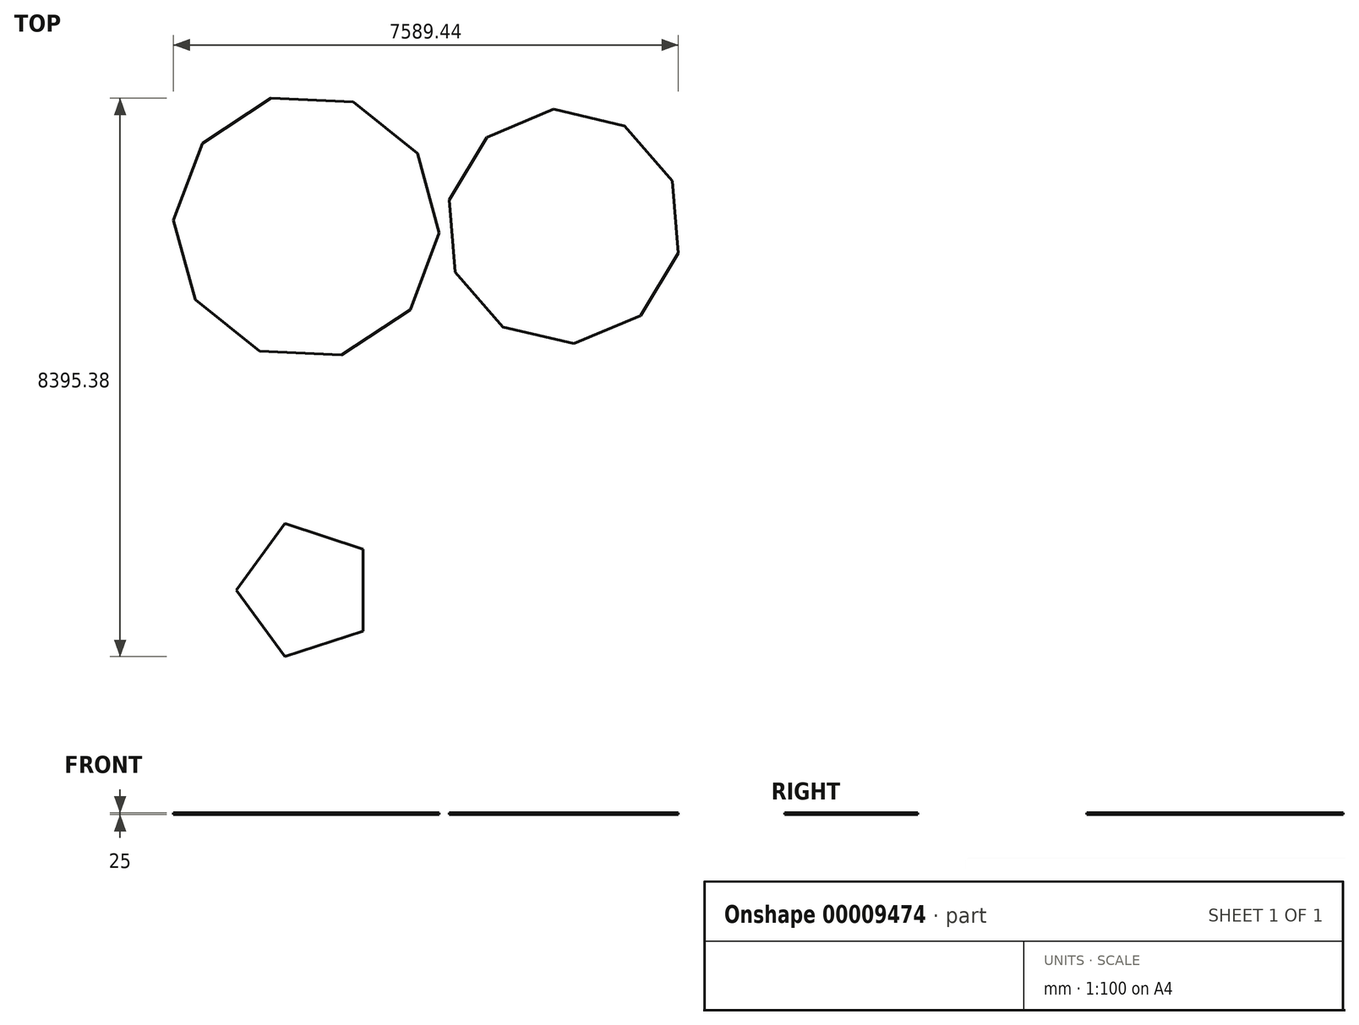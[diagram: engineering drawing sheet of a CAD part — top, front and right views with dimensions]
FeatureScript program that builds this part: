
annotation { "Feature Type Name" : "Feature", "Feature Type Description" : "" }
export const myFeature = defineFeature(function(context is Context, id is Id, definition is map)
    precondition{}
    {
        {
            var Q0;
            Q0=qCreatedBy(makeId("Top.planeOp"),FACE);
            var sketch = newSketch(context, id + "F0", { "sketchPlane" : qUnion([Q0])});
            skCircle(sketch, "E0.cCircle", {"center": v(0, 0) * mm, "radius": 1902 * mm, "construction": true});
            skLineSegment(sketch, "E0.0", {"start": v(1997.74, -92.8) * mm, "end": v(1561.66, -1249.31) * mm});
            skLineSegment(sketch, "E0.1", {"start": v(1561.66, -1249.31) * mm, "end": v(529.08, -1928.63) * mm});
            skLineSegment(sketch, "E0.2", {"start": v(529.08, -1928.63) * mm, "end": v(-705.59, -1871.28) * mm});
            skLineSegment(sketch, "E0.3", {"start": v(-705.59, -1871.28) * mm, "end": v(-1670.75, -1099.17) * mm});
            skLineSegment(sketch, "E0.4", {"start": v(-1670.75, -1099.17) * mm, "end": v(-1997.74, 92.8) * mm});
            skLineSegment(sketch, "E0.5", {"start": v(-1997.74, 92.8) * mm, "end": v(-1561.66, 1249.31) * mm});
            skLineSegment(sketch, "E0.6", {"start": v(-1561.66, 1249.31) * mm, "end": v(-529.08, 1928.63) * mm});
            skLineSegment(sketch, "E0.7", {"start": v(-529.08, 1928.63) * mm, "end": v(705.59, 1871.28) * mm});
            skLineSegment(sketch, "E0.8", {"start": v(705.59, 1871.28) * mm, "end": v(1670.75, 1099.17) * mm});
            skLineSegment(sketch, "E0.9", {"start": v(1670.75, 1099.17) * mm, "end": v(1997.74, -92.8) * mm});
            skPoint(sketch, "E0.0.midPoint", {"position": v(1779.7, -671.05) * mm});
            skSolve(sketch);
        }
        {
            var Q0;
            Q0=makeQuery(id+"F0.imprint","IMPRINT",FACE,{"disambiguationData":[TD([[makeQuery(id+"F0.imprint","IMPRINT",EDGE,{"derivedFrom":sQuery(id+"F0.wireOp",EDGE,"E0.0")}),-1.0]])]});
            extrude(context, id + "F1", {"entities" : qUnion([Q0]), "depth" : 25 * mm});
        }
        {
            var Q0;
            Q0=qCreatedBy(makeId("Top.planeOp"),FACE);
            var sketch = newSketch(context, id + "F2", { "sketchPlane" : qUnion([Q0])});
            skCircle(sketch, "E1.cCircle", {"center": v(3869.29, 0) * mm, "radius": 1681.95 * mm, "construction": true});
            skLineSegment(sketch, "E1.0", {"start": v(5591.7, -401.14) * mm, "end": v(5026.97, -1336.94) * mm});
            skLineSegment(sketch, "E1.1", {"start": v(5026.97, -1336.94) * mm, "end": v(4020.04, -1762.07) * mm});
            skLineSegment(sketch, "E1.2", {"start": v(4020.04, -1762.07) * mm, "end": v(2955.53, -1514.16) * mm});
            skLineSegment(sketch, "E1.3", {"start": v(2955.53, -1514.16) * mm, "end": v(2240.04, -687.89) * mm});
            skLineSegment(sketch, "E1.4", {"start": v(2240.04, -687.89) * mm, "end": v(2146.87, 401.14) * mm});
            skLineSegment(sketch, "E1.5", {"start": v(2146.87, 401.14) * mm, "end": v(2711.6, 1336.94) * mm});
            skLineSegment(sketch, "E1.6", {"start": v(2711.6, 1336.94) * mm, "end": v(3718.53, 1762.07) * mm});
            skLineSegment(sketch, "E1.7", {"start": v(3718.53, 1762.07) * mm, "end": v(4783.05, 1514.16) * mm});
            skLineSegment(sketch, "E1.8", {"start": v(4783.05, 1514.16) * mm, "end": v(5498.53, 687.89) * mm});
            skLineSegment(sketch, "E1.9", {"start": v(5498.53, 687.89) * mm, "end": v(5591.7, -401.14) * mm});
            skPoint(sketch, "E1.0.midPoint", {"position": v(5309.34, -869.04) * mm});
            skSolve(sketch);
        }
        {
            var Q0;
            Q0=makeQuery(id+"F2.imprint","IMPRINT",FACE,{"disambiguationData":[TD([[makeQuery(id+"F2.imprint","IMPRINT",EDGE,{"derivedFrom":sQuery(id+"F2.wireOp",EDGE,"E1.0")}),-1.0]])]});
            extrude(context, id + "F3", {"entities" : qUnion([Q0]), "depth" : 25 * mm});
        }
        {
            var Q0;
            Q0=qCreatedBy(makeId("Top.planeOp"),FACE);
            var sketch = newSketch(context, id + "F4", { "sketchPlane" : qUnion([Q0])});
            skCircle(sketch, "E2.cCircle", {"center": v(0, -5466.8) * mm, "radius": 850.6 * mm, "construction": true});
            skLineSegment(sketch, "E2.0", {"start": v(850.6, -4848.8) * mm, "end": v(850.6, -6084.8) * mm});
            skLineSegment(sketch, "E2.1", {"start": v(850.6, -6084.8) * mm, "end": v(-324.9, -6466.75) * mm});
            skLineSegment(sketch, "E2.2", {"start": v(-324.9, -6466.75) * mm, "end": v(-1051.4, -5466.8) * mm});
            skLineSegment(sketch, "E2.3", {"start": v(-1051.4, -5466.8) * mm, "end": v(-324.9, -4466.86) * mm});
            skLineSegment(sketch, "E2.4", {"start": v(-324.9, -4466.86) * mm, "end": v(850.6, -4848.8) * mm});
            skPoint(sketch, "E2.0.midPoint", {"position": v(850.6, -5466.8) * mm});
            skSolve(sketch);
        }
        {
            var Q0;
            Q0 = qSketchRegion(id + "F4", true);
            extrude(context, id + "F5", {"entities" : qUnion([Q0]), "depth" : 25 * mm});
        }
    });
